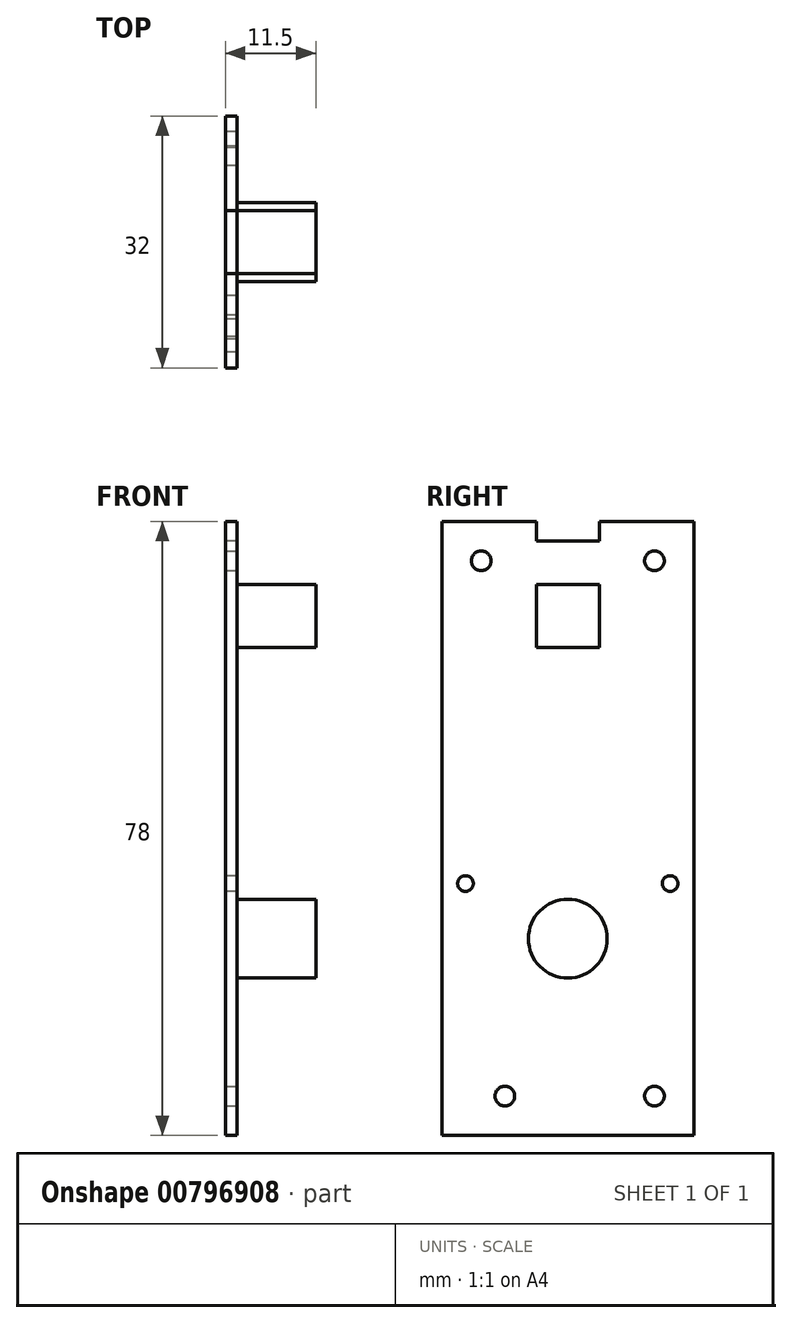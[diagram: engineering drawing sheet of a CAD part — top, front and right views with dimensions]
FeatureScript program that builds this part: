
annotation { "Feature Type Name" : "Feature", "Feature Type Description" : "" }
export const myFeature = defineFeature(function(context is Context, id is Id, definition is map)
    precondition{}
    {
        {
            var Q0;
            Q0=qCreatedBy(makeId("Right.planeOp"),FACE);
            var sketch = newSketch(context, id + "F0", { "sketchPlane" : qUnion([Q0])});
            skLineSegment(sketch, "E0.bottom", {"start": v(0, 0) * mm, "end": v(32, 0) * mm});
            skLineSegment(sketch, "E0.left", {"start": v(0, 0) * mm, "end": v(0, 78) * mm});
            skLineSegment(sketch, "E0.right", {"start": v(32, 0) * mm, "end": v(32, 78) * mm});
            skCircle(sketch, "E1", {"center": v(16, 26) * mm, "radius": 5 * mm, "construction": true});
            skCircle(sketch, "E2", {"center": v(29, 32) * mm, "radius": 1 * mm});
            skCircle(sketch, "E3", {"center": v(3, 32) * mm, "radius": 1 * mm});
            skLineSegment(sketch, "E4", {"start": v(20, 78) * mm, "end": v(20, 75.5) * mm});
            skLineSegment(sketch, "E5", {"start": v(20, 75.5) * mm, "end": v(12, 75.5) * mm});
            skLineSegment(sketch, "E6", {"start": v(12, 75.5) * mm, "end": v(12, 78) * mm});
            skLineSegment(sketch, "E7", {"start": v(0, 78) * mm, "end": v(12, 78) * mm});
            skLineSegment(sketch, "E8", {"start": v(20, 78) * mm, "end": v(32, 78) * mm});
            skSolve(sketch);
        }
        {
            var Q0;
            Q0=makeQuery(id+"F0.imprint","IMPRINT",FACE,{"disambiguationData":[TD([[makeQuery(id+"F0.imprint","IMPRINT",EDGE,{"derivedFrom":sQuery(id+"F0.wireOp",EDGE,"E0.bottom")}),1.0]])]});
            extrude(context, id + "F1", {"entities" : qUnion([Q0]), "depth" : 1.5 * mm, "offsetDistance" : 25 * mm});
        }
        {
            var Q0;
            Q0=makeQuery(id+"F1.opExtrude","CAP_FACE",FACE,{"disambiguationData":[OSD([sQuery(id+"F0.wireOp",EDGE,"E0.bottom"),sQuery(id+"F0.wireOp",EDGE,"E0.left"),sQuery(id+"F0.wireOp",EDGE,"E0.right"),sQuery(id+"F0.wireOp",EDGE,"E2"),sQuery(id+"F0.wireOp",EDGE,"E3"),sQuery(id+"F0.wireOp",EDGE,"E4"),sQuery(id+"F0.wireOp",EDGE,"E5"),sQuery(id+"F0.wireOp",EDGE,"E6"),sQuery(id+"F0.wireOp",EDGE,"E7"),sQuery(id+"F0.wireOp",EDGE,"E8")])],"isStart":false});
            var sketch = newSketch(context, id + "F2", { "sketchPlane" : qUnion([Q0])});
            skCircle(sketch, "E9", {"center": v(16, 25) * mm, "radius": 5 * mm});
            skSolve(sketch);
        }
        {
            var Q0;
            Q0=makeQuery(id+"F2.imprint","IMPRINT",FACE,{"disambiguationData":[TD([[makeQuery(id+"F2.imprint","IMPRINT",EDGE,{"derivedFrom":sQuery(id+"F2.wireOp",EDGE,"E9")}),1.0]])]});
            extrude(context, id + "F3", {"entities" : qUnion([Q0]), "operationType" : NewBodyOperationType.ADD, "depth" : 10 * mm, "offsetDistance" : 25 * mm});
        }
        {
            var Q0;
            Q0=makeQuery(id+"F1.opExtrude","CAP_FACE",FACE,{"disambiguationData":[OSD([sQuery(id+"F0.wireOp",EDGE,"E0.bottom"),sQuery(id+"F0.wireOp",EDGE,"E0.left"),sQuery(id+"F0.wireOp",EDGE,"E0.right"),sQuery(id+"F0.wireOp",EDGE,"E2"),sQuery(id+"F0.wireOp",EDGE,"E3"),sQuery(id+"F0.wireOp",EDGE,"E4"),sQuery(id+"F0.wireOp",EDGE,"E5"),sQuery(id+"F0.wireOp",EDGE,"E6"),sQuery(id+"F0.wireOp",EDGE,"E7"),sQuery(id+"F0.wireOp",EDGE,"E8")])],"isStart":false});
            var sketch = newSketch(context, id + "F4", { "sketchPlane" : qUnion([Q0])});
            skPoint(sketch, "E10.startSnap0", {"position": v(16, 75.5) * mm});
            skLineSegment(sketch, "E11", {"start": v(16, 70) * mm, "end": v(12, 70) * mm});
            skLineSegment(sketch, "E12", {"start": v(12, 70) * mm, "end": v(12, 62) * mm});
            skLineSegment(sketch, "E13", {"start": v(12, 62) * mm, "end": v(20, 62) * mm});
            skLineSegment(sketch, "E14", {"start": v(20, 62) * mm, "end": v(20, 70) * mm});
            skLineSegment(sketch, "E15", {"start": v(20, 70) * mm, "end": v(16, 70) * mm});
            skSolve(sketch);
        }
        {
            var Q0;
            Q0=makeQuery(id+"F4.imprint","IMPRINT",FACE,{"disambiguationData":[TD([[makeQuery(id+"F4.imprint","IMPRINT",EDGE,{"derivedFrom":sQuery(id+"F4.wireOp",EDGE,"E11")}),1.0]])]});
            extrude(context, id + "F5", {"entities" : qUnion([Q0]), "operationType" : NewBodyOperationType.ADD, "depth" : 10 * mm, "offsetDistance" : 25 * mm});
        }
        {
            var Q0;
            Q0=makeQuery(id+"F1.opExtrude","CAP_FACE",FACE,{"disambiguationData":[OSD([sQuery(id+"F0.wireOp",EDGE,"E0.bottom"),sQuery(id+"F0.wireOp",EDGE,"E0.left"),sQuery(id+"F0.wireOp",EDGE,"E0.right"),sQuery(id+"F0.wireOp",EDGE,"E2"),sQuery(id+"F0.wireOp",EDGE,"E3"),sQuery(id+"F0.wireOp",EDGE,"E4"),sQuery(id+"F0.wireOp",EDGE,"E5"),sQuery(id+"F0.wireOp",EDGE,"E6"),sQuery(id+"F0.wireOp",EDGE,"E7"),sQuery(id+"F0.wireOp",EDGE,"E8")])],"isStart":false});
            var sketch = newSketch(context, id + "F6", { "sketchPlane" : qUnion([Q0])});
            skCircle(sketch, "E16", {"center": v(27, 73) * mm, "radius": 1.25 * mm});
            skCircle(sketch, "E17", {"center": v(5, 73) * mm, "radius": 1.25 * mm});
            skCircle(sketch, "E18", {"center": v(27, 5) * mm, "radius": 1.25 * mm});
            skCircle(sketch, "E19", {"center": v(8, 5) * mm, "radius": 1.25 * mm});
            skSolve(sketch);
        }
        {
            var Q0;
            Q0=sQuery(id+"F6.wireOp",VERTEX,"E17.center");
            var Q1;
            Q1=sQuery(id+"F6.wireOp",VERTEX,"E16.center");
            var Q2;
            Q2=sQuery(id+"F6.wireOp",VERTEX,"E18.center");
            var Q3;
            Q3=sQuery(id+"F6.wireOp",VERTEX,"E19.center");
            var Q4;
            Q4=makeQuery(id+"F1.opExtrude","SWEPT_BODY",BODY,{"disambiguationData":[OSD([sQuery(id+"F0.wireOp",EDGE,"E0.bottom"),sQuery(id+"F0.wireOp",EDGE,"E0.left"),sQuery(id+"F0.wireOp",EDGE,"E0.right"),sQuery(id+"F0.wireOp",EDGE,"E2"),sQuery(id+"F0.wireOp",EDGE,"E3"),sQuery(id+"F0.wireOp",EDGE,"E4"),sQuery(id+"F0.wireOp",EDGE,"E5"),sQuery(id+"F0.wireOp",EDGE,"E6"),sQuery(id+"F0.wireOp",EDGE,"E7"),sQuery(id+"F0.wireOp",EDGE,"E8")])]});
            hole(context, id + "F7", {"style" : HoleStyle.SIMPLE, "endStyle" : HoleEndStyle.THROUGH, "holeDiameter" : 2.5 * mm, "majorDiameter" : 5 * mm, "isTappedThrough" : true, "tappedDepth" : 12 * mm, "tapClearance" : 3, "locations" : qUnion([Q0, Q1, Q2, Q3]), "scope" : qUnion([Q4])});
        }
    });
